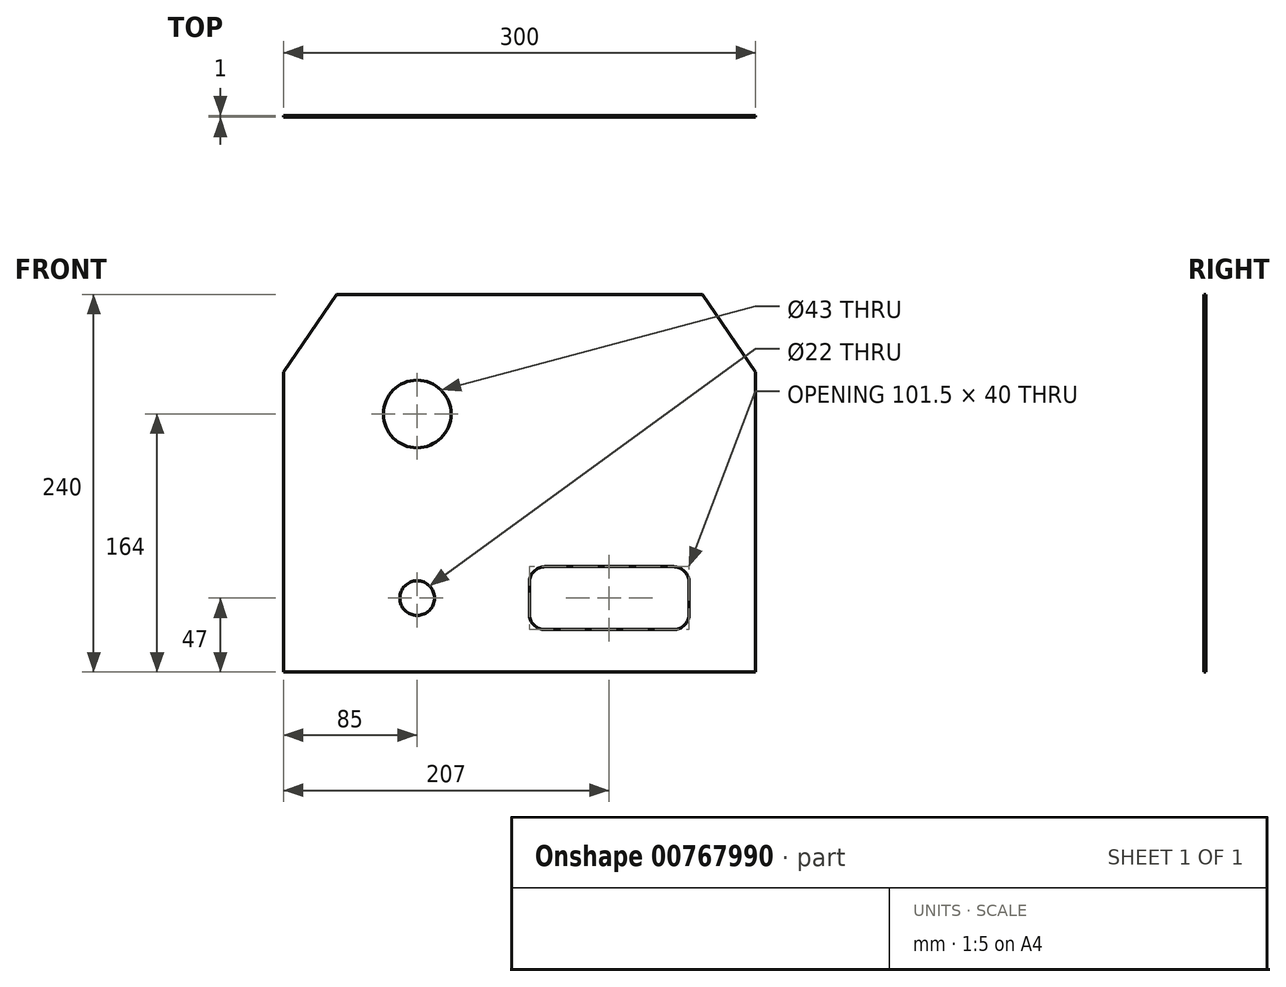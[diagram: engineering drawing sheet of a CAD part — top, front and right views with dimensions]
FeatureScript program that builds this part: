
annotation { "Feature Type Name" : "Feature", "Feature Type Description" : "" }
export const myFeature = defineFeature(function(context is Context, id is Id, definition is map)
    precondition{}
    {
        {
            var Q0;
            Q0=qCreatedBy(makeId("Front.planeOp"),FACE);
            var sketch = newSketch(context, id + "F0", { "sketchPlane" : qUnion([Q0])});
            skLineSegment(sketch, "E0.bottom", {"start": v(150, -120) * mm, "end": v(-150, -120) * mm});
            skLineSegment(sketch, "E0.top", {"start": v(116.21, 120) * mm, "end": v(-116.21, 120) * mm});
            skLineSegment(sketch, "E0.left", {"start": v(150, -120) * mm, "end": v(150, 70.5) * mm});
            skLineSegment(sketch, "E0.right", {"start": v(-150, -120) * mm, "end": v(-150, 70.5) * mm});
            skPoint(sketch, "E0.middle", {"position": v(0, 0) * mm});
            skLineSegment(sketch, "E1", {"start": v(-150, 70.5) * mm, "end": v(-116.21, 120) * mm});
            skPoint(sketch, "E2.orphan", {"position": v(-150, 120) * mm});
            skLineSegment(sketch, "E3", {"start": v(116.21, 120) * mm, "end": v(150, 70.5) * mm});
            skPoint(sketch, "E4.orphan", {"position": v(150, 120) * mm});
            skCircle(sketch, "E5", {"center": v(-65, 44) * mm, "radius": 21.5 * mm});
            skCircle(sketch, "E6", {"center": v(-65, -73) * mm, "radius": 11 * mm});
            skLineSegment(sketch, "E7", {"start": v(-65, 44) * mm, "end": v(-65, -152.23) * mm, "construction": true});
            skLineSegment(sketch, "E8.bottom", {"start": v(97.75, -93) * mm, "end": v(16.25, -93) * mm});
            skLineSegment(sketch, "E8.top", {"start": v(97.75, -53) * mm, "end": v(16.25, -53) * mm});
            skLineSegment(sketch, "E8.left", {"start": v(107.75, -83) * mm, "end": v(107.75, -63) * mm});
            skLineSegment(sketch, "E8.right", {"start": v(6.25, -83) * mm, "end": v(6.25, -63) * mm});
            skPoint(sketch, "E8.middle", {"position": v(57, -73) * mm});
            skPoint(sketch, "E9.visualSharp", {"position": v(6.25, -53) * mm});
            skArc(sketch, "E9.filletArc", {"start": v(16.25, -53) * mm, "mid": v(9.18, -55.93) * mm, "end": v(6.25, -63) * mm});
            skPoint(sketch, "E10.visualSharp", {"position": v(107.75, -53) * mm});
            skArc(sketch, "E10.filletArc", {"start": v(107.75, -63) * mm, "mid": v(104.82, -55.93) * mm, "end": v(97.75, -53) * mm});
            skPoint(sketch, "E11.visualSharp", {"position": v(107.75, -93) * mm});
            skArc(sketch, "E11.filletArc", {"start": v(97.75, -93) * mm, "mid": v(104.82, -90.07) * mm, "end": v(107.75, -83) * mm});
            skPoint(sketch, "E12.visualSharp", {"position": v(6.25, -93) * mm});
            skArc(sketch, "E12.filletArc", {"start": v(6.25, -83) * mm, "mid": v(9.18, -90.07) * mm, "end": v(16.25, -93) * mm});
            skSolve(sketch);
        }
        {
            var Q0;
            Q0=makeQuery(id+"F0.imprint","IMPRINT",FACE,{"disambiguationData":[TD([[makeQuery(id+"F0.imprint","IMPRINT",EDGE,{"derivedFrom":sQuery(id+"F0.wireOp",EDGE,"E0.bottom")}),-1.0]])]});
            extrude(context, id + "F1", {"entities" : qUnion([Q0]), "depth" : 1 * mm, "offsetDistance" : 25 * mm});
        }
    });
